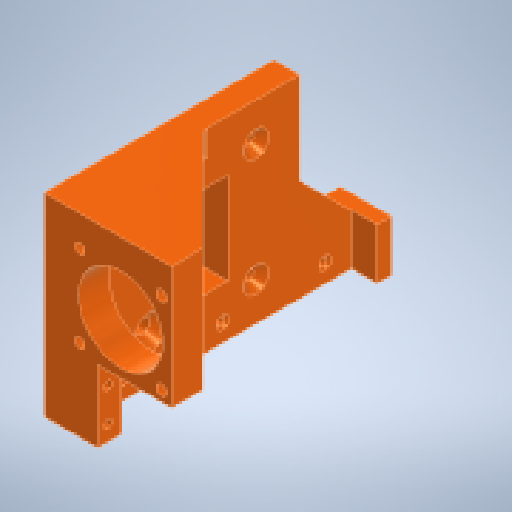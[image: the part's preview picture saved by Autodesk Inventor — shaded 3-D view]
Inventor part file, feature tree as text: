
AUTODESK INVENTOR PART (.ipt)
format: ipt  version: 2024.1 (Build 281209000, 209)  size: 332,800 bytes
history: native  units: in
note: dims shown in document units (in); Inventor stores cm internally (conversion verified against a paired STEP export)
features: extrude x15, sketch x15, chamfer x5, fillet x1
ambient origin geometry x8: Origin, YZ Plane, XZ Plane, XY Plane, X Axis, Y Axis, Z Axis, Center Point
bodies: Solid1 (feature_tree)
feature tree (36):
  extrude  "Extrusion1"  Depth=1.4961in
  extrude  "Extrusion2"  Depth=0.9449in
  extrude  "Extrusion3"  Depth=0.7874in TaperAngle=0.0deg
  extrude  "Extrusion4"  Depth=0.3937in
  extrude  "Extrusion5"  Depth=0.3937in
  fillet  "Fillet1"  Radius=0.0787in
  extrude  "Extrusion6"  Depth=0.0787in
  extrude  "Extrusion7"  Depth=0.315in
  chamfer  "Chamfer1"  [1 undecoded]
  chamfer  "Chamfer2"  Distance=0.7874in
  extrude  "Extrusion8"  Depth=0.0197in
  chamfer  "Chamfer3"  Distance=0.0787in
  extrude  "Extrusion9"  Depth=0.7087in
  chamfer  "Chamfer4"  Distance=1.378in
  extrude  "Extrusion10"  TaperAngle=0.0deg  [1 undecoded]
  extrude  "Extrusion15"  Depth=0.0197in
  extrude  "Extrusion16"  Depth=0.0197in
  extrude  "Extrusion17"  Depth=0.1575in
  extrude  "Extrusion18"  Depth=0.0197in
  extrude  "Extrusion19"  Depth=0.0197in
  chamfer  "Chamfer5"  Distance=0.1575in
  sketch  "Sketch1"  dims[d0=1.4961in d1=2.1654in]
  sketch  "Sketch2"  dims[d2=0.1969in d3=0.0in d4=0.9449in]
  sketch  "Sketch3"  dims[d5=0.2362in d6=0.7874in d7=0.0in]
  sketch  "Sketch4"  dims[d8=0.6496in d9=0.3937in]
  sketch  "Sketch5"  dims[d10=0.3937in d11=0.0787in d12=0.0787in]
  sketch  "Sketch6"  dims[d13=0.0787in d14=0.0787in]
  sketch  "Sketch7"  dims[d15=0.315in d16=0.315in]
  sketch  "Sketch8"  dims[d17=0.315in]
  sketch  "Sketch9"  dims[d18=0.315in]
  sketch  "Sketch10"  dims[d19=0.315in]
  sketch  "Sketch15"  dims[d20=0.315in]
  sketch  "Sketch16"  dims[d21=0.315in]
  sketch  "Sketch17"  dims[d22=0.315in d23=0.0in d24=0.0in]
  sketch  "Sketch18"  dims[d25=0.1181in d26=0.7874in d27=0.0in]
  sketch  "Sketch19"  dims[d28=0.0in d29=0.0in d30=0.0787in d31=0.0787in d32=0.7087in d33=1.378in d34=0.0in d35=0.0in d36=0.1181in d37=0.1181in d38=0.1575in d39=0.4331in d40=0.4331in d41=0.1575in d42=0.0in d43=0.0in d44=0.0591in d45=0.0787in d46=45.0deg d47=0.0748in d48=0.0787in d49=45.0deg d50=1.1024in d51=0.3937in d52=0.0in d53=0.0in d54=0.3937in d55=0.0787in d56=45.0deg d57=0.0787in d58=0.0787in d59=0.2953in d60=0.7283in d61=0.2953in d62=0.7283in d63=0.0in d64=0.0in d65=0.0591in d66=0.0787in d67=45.0deg d68=0.0591in d69=0.0591in d70=0.0591in d71=0.1378in d72=0.1969in d73=0.1378in d74=0.7874in d76=0.1378in d77=0.0in d78=0.0in d95=0.7874in d96=0.1181in d97=0.3937in d98=0.2165in d99=0.0in d100=0.1102in d101=0.1969in d102=0.0in d103=0.189in d104=0.2165in d105=0.0in d106=0.0591in d107=0.0591in d108=0.2559in d109=0.1181in d110=0.0787in d111=0.0787in d112=0.0in d113=0.0in d114=0.1969in d115=0.3937in d116=0.3937in d117=0.5512in d118=0.0in d119=0.0in d120=0.0197in d121=0.0787in d122=45.0deg]
note: 2 required parameter values undecoded (feature->parameter linkage not recoverable at this tier; creation-order binding heuristic only, values carry confidence <= 0.55)
